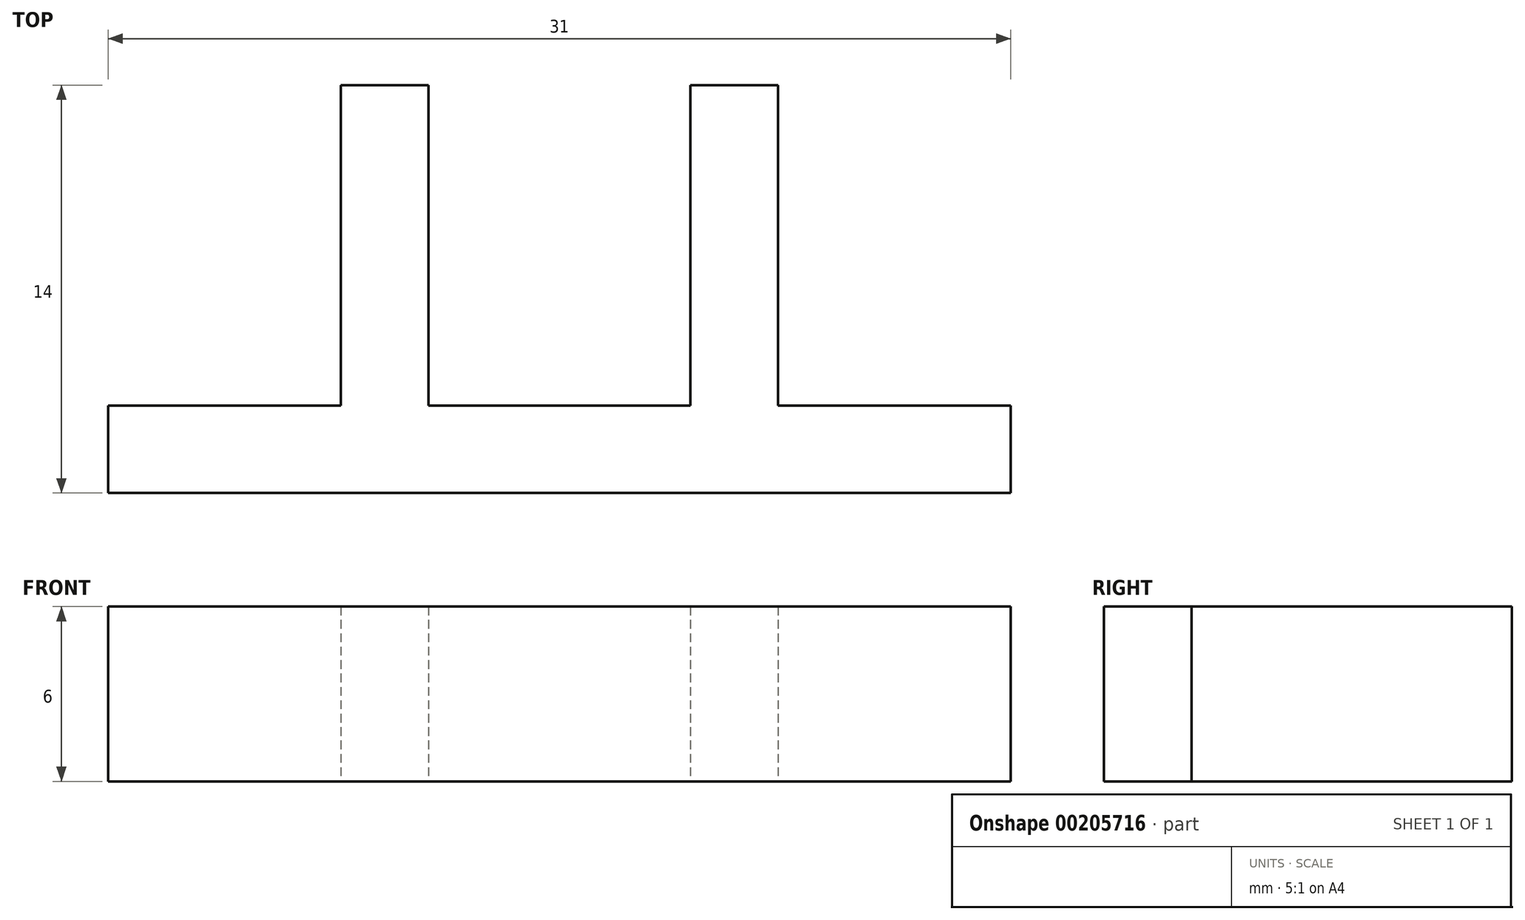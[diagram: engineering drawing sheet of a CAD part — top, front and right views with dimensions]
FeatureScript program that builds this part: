
annotation { "Feature Type Name" : "Feature", "Feature Type Description" : "" }
export const myFeature = defineFeature(function(context is Context, id is Id, definition is map)
    precondition{}
    {
        {
            var Q0;
            Q0=qCreatedBy(makeId("Top.planeOp"),FACE);
            var sketch = newSketch(context, id + "F0", { "sketchPlane" : qUnion([Q0])});
            skLineSegment(sketch, "E0", {"start": v(0, 0) * mm, "end": v(31, 0) * mm});
            skLineSegment(sketch, "E1", {"start": v(31, 0) * mm, "end": v(31, 3) * mm});
            skLineSegment(sketch, "E2", {"start": v(31, 3) * mm, "end": v(23, 3) * mm});
            skLineSegment(sketch, "E3", {"start": v(23, 3) * mm, "end": v(23, 14) * mm});
            skLineSegment(sketch, "E4", {"start": v(23, 14) * mm, "end": v(20, 14) * mm});
            skLineSegment(sketch, "E5", {"start": v(20, 14) * mm, "end": v(20, 3) * mm});
            skLineSegment(sketch, "E6", {"start": v(20, 3) * mm, "end": v(11, 3) * mm});
            skLineSegment(sketch, "E7", {"start": v(11, 3) * mm, "end": v(11, 14) * mm});
            skLineSegment(sketch, "E8", {"start": v(11, 14) * mm, "end": v(8, 14) * mm});
            skLineSegment(sketch, "E9", {"start": v(8, 14) * mm, "end": v(8, 3) * mm});
            skLineSegment(sketch, "E10", {"start": v(8, 3) * mm, "end": v(0, 3) * mm});
            skLineSegment(sketch, "E11", {"start": v(0, 3) * mm, "end": v(0, 0) * mm});
            skSolve(sketch);
        }
        {
            var Q0;
            Q0=makeQuery(id+"F0.imprint","IMPRINT",FACE,{"disambiguationData":[TD([[makeQuery(id+"F0.imprint","IMPRINT",EDGE,{"derivedFrom":sQuery(id+"F0.wireOp",EDGE,"E0")}),1.0]])]});
            extrude(context, id + "F1", {"entities" : qUnion([Q0]), "depth" : 6 * mm});
        }
    });
